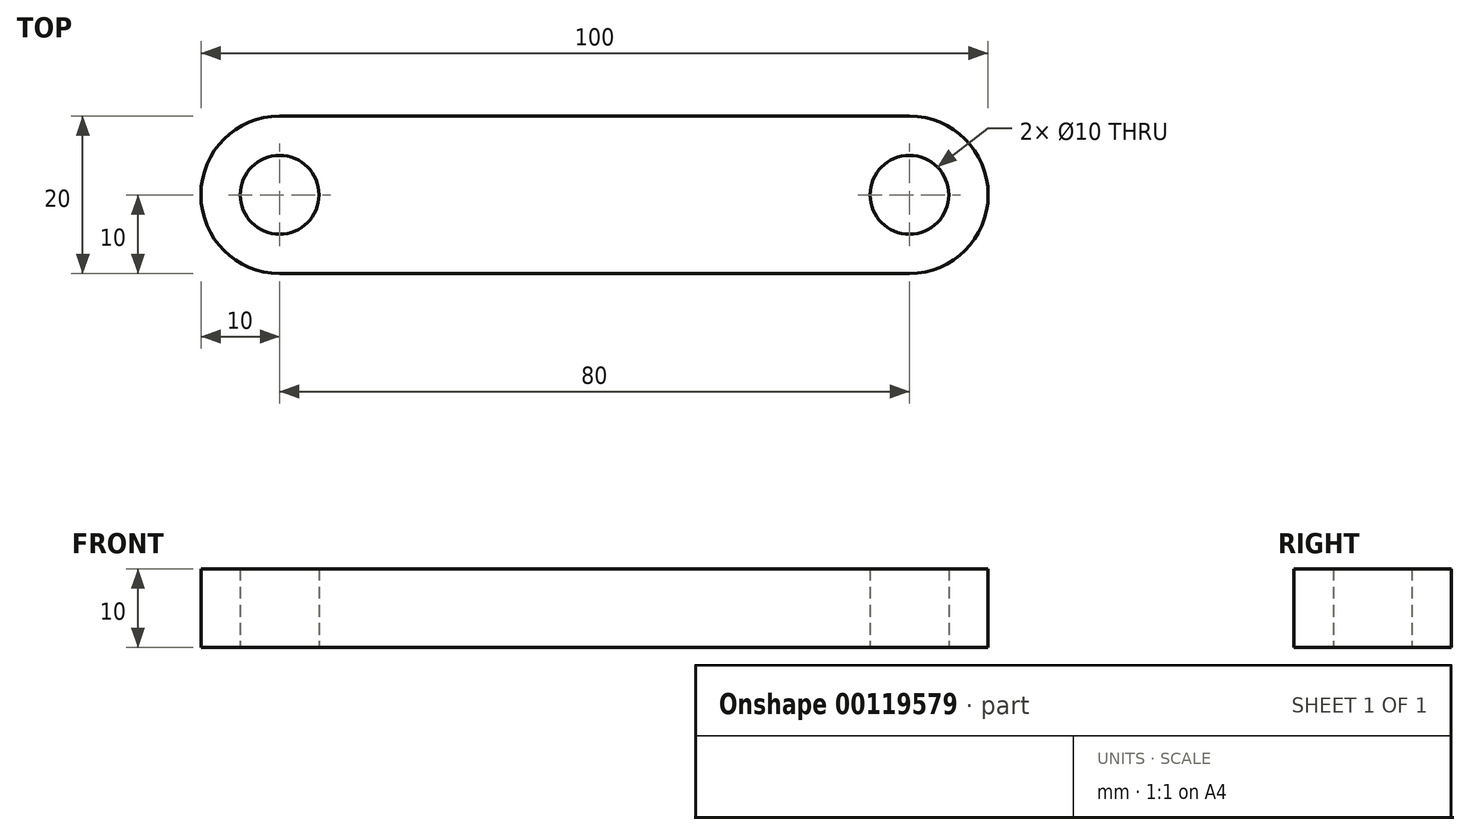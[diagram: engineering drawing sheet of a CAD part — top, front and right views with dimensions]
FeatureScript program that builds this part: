
annotation { "Feature Type Name" : "Feature", "Feature Type Description" : "" }
export const myFeature = defineFeature(function(context is Context, id is Id, definition is map)
    precondition{}
    {
        {
            var Q0;
            Q0=qCreatedBy(makeId("Top.planeOp"),FACE);
            var sketch = newSketch(context, id + "F0", { "sketchPlane" : qUnion([Q0])});
            skLineSegment(sketch, "E0.bottom", {"start": v(0, 0) * mm, "end": v(80, 0) * mm});
            skLineSegment(sketch, "E0.top", {"start": v(0, 20) * mm, "end": v(80, 20) * mm});
            skArc(sketch, "E1", {"start": v(0, 20) * mm, "mid": v(-10, 10) * mm, "end": v(0, 0) * mm});
            skArc(sketch, "E2", {"start": v(80, 20) * mm, "mid": v(90, 10) * mm, "end": v(80, 0) * mm});
            skCircle(sketch, "E3", {"center": v(0, 10) * mm, "radius": 5 * mm});
            skCircle(sketch, "E4", {"center": v(80, 10) * mm, "radius": 5 * mm});
            skSolve(sketch);
        }
        {
            var Q0;
            Q0 = qSketchRegion(id + "F0", true);
            extrude(context, id + "F1", {"entities" : qUnion([Q0]), "depth" : 10 * mm});
        }
    });
